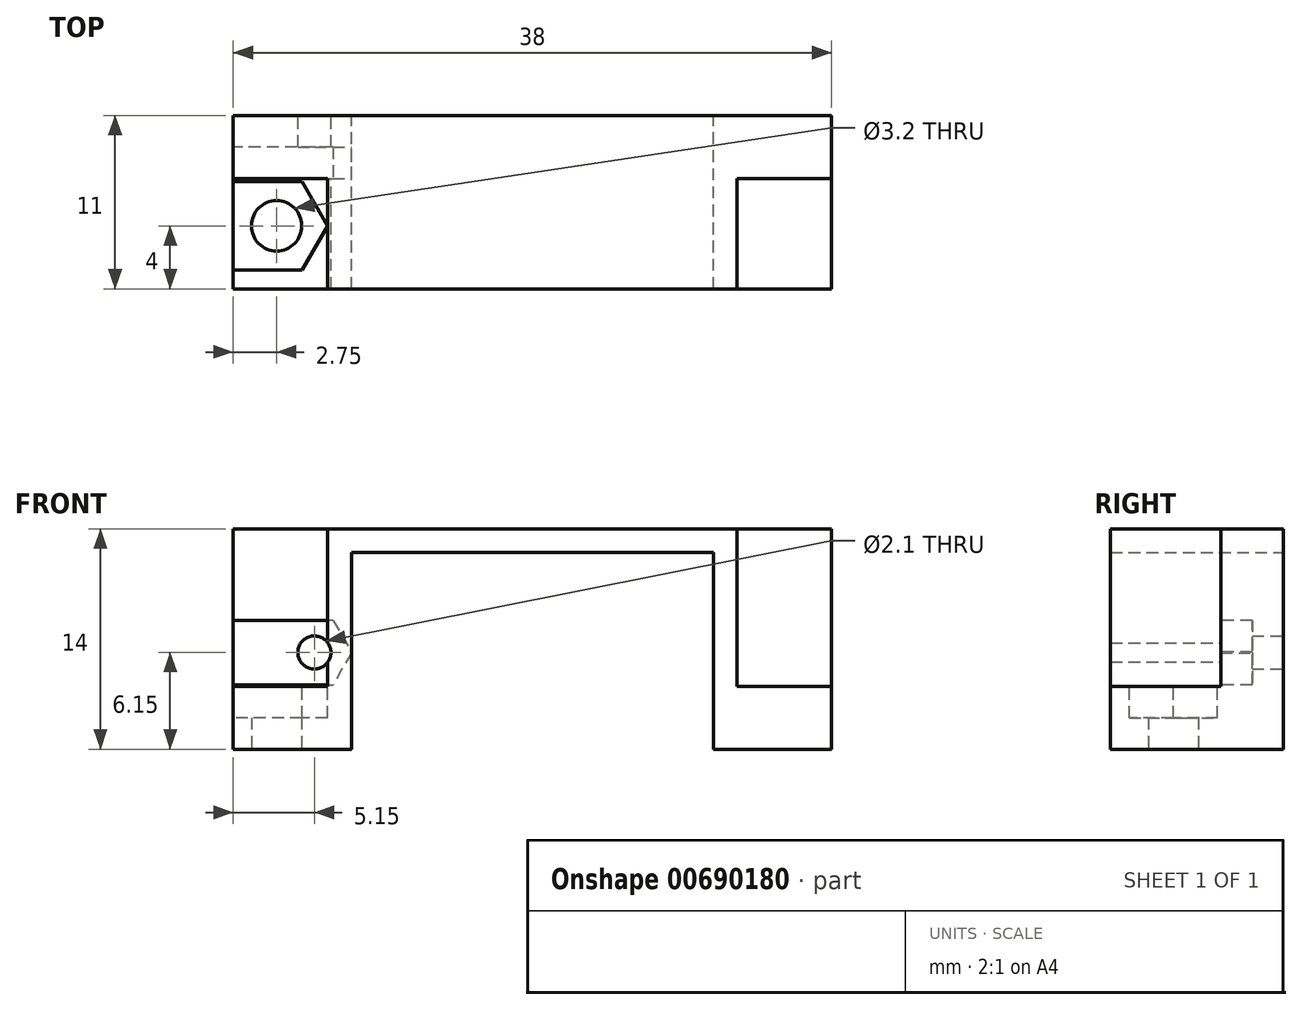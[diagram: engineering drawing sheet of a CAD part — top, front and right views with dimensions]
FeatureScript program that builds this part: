
annotation { "Feature Type Name" : "Feature", "Feature Type Description" : "" }
export const myFeature = defineFeature(function(context is Context, id is Id, definition is map)
    precondition{}
    {
        {
            var Q0;
            Q0=qCreatedBy(makeId("Front.planeOp"),FACE);
            var sketch = newSketch(context, id + "F0", { "sketchPlane" : qUnion([Q0])});
            skLineSegment(sketch, "E0", {"start": v(-19, 0) * mm, "end": v(-19, 4) * mm});
            skLineSegment(sketch, "E1", {"start": v(-19, 4) * mm, "end": v(-13, 4) * mm});
            skLineSegment(sketch, "E2", {"start": v(-13, 4) * mm, "end": v(-13, 14) * mm});
            skLineSegment(sketch, "E3", {"start": v(-13, 14) * mm, "end": v(13, 14) * mm});
            skLineSegment(sketch, "E4", {"start": v(13, 14) * mm, "end": v(13, 4) * mm});
            skLineSegment(sketch, "E5", {"start": v(13, 4) * mm, "end": v(19, 4) * mm});
            skLineSegment(sketch, "E6", {"start": v(19, 4) * mm, "end": v(19, 0) * mm});
            skLineSegment(sketch, "E7", {"start": v(19, 0) * mm, "end": v(11.5, 0) * mm});
            skLineSegment(sketch, "E8", {"start": v(-11.5, 0) * mm, "end": v(-11.5, 12.5) * mm});
            skLineSegment(sketch, "E9", {"start": v(-11.5, 12.5) * mm, "end": v(11.5, 12.5) * mm});
            skLineSegment(sketch, "E10", {"start": v(11.5, 12.5) * mm, "end": v(11.5, 0) * mm});
            skLineSegment(sketch, "E11.trimOffspring", {"start": v(-11.5, 0) * mm, "end": v(-19, 0) * mm});
            skSolve(sketch);
        }
        {
            var Q0;
            Q0=makeQuery(id+"F0.imprint","IMPRINT",FACE,{"disambiguationData":[TD([[makeQuery(id+"F0.imprint","IMPRINT",EDGE,{"derivedFrom":sQuery(id+"F0.wireOp",EDGE,"E0")}),-1.0]])]});
            extrude(context, id + "F1", {"entities" : qUnion([Q0]), "depth" : 11 * mm, "offsetDistance" : 25 * mm});
        }
        {
            var Q0;
            Q0=makeQuery(id+"F1.opExtrude","CAP_FACE",FACE,{"disambiguationData":[OSD([sQuery(id+"F0.wireOp",EDGE,"E0"),sQuery(id+"F0.wireOp",EDGE,"E1"),sQuery(id+"F0.wireOp",EDGE,"E2"),sQuery(id+"F0.wireOp",EDGE,"E3"),sQuery(id+"F0.wireOp",EDGE,"E4"),sQuery(id+"F0.wireOp",EDGE,"E5"),sQuery(id+"F0.wireOp",EDGE,"E6"),sQuery(id+"F0.wireOp",EDGE,"E7"),sQuery(id+"F0.wireOp",EDGE,"E8"),sQuery(id+"F0.wireOp",EDGE,"E9"),sQuery(id+"F0.wireOp",EDGE,"E10"),sQuery(id+"F0.wireOp",EDGE,"E11.trimOffspring")])],"isStart":true});
            var sketch = newSketch(context, id + "F2", { "sketchPlane" : qUnion([Q0])});
            skLineSegment(sketch, "E12.bottom", {"start": v(11.5, 0) * mm, "end": v(19, 0) * mm});
            skLineSegment(sketch, "E12.top", {"start": v(11.5, 14) * mm, "end": v(19, 14) * mm});
            skLineSegment(sketch, "E12.left", {"start": v(11.5, 0) * mm, "end": v(11.5, 14) * mm});
            skLineSegment(sketch, "E12.right", {"start": v(19, 0) * mm, "end": v(19, 14) * mm});
            skLineSegment(sketch, "E13.bottom", {"start": v(-11.5, 0) * mm, "end": v(-19, 0) * mm});
            skLineSegment(sketch, "E13.top", {"start": v(-11.5, 14) * mm, "end": v(-19, 14) * mm});
            skLineSegment(sketch, "E13.left", {"start": v(-11.5, 0) * mm, "end": v(-11.5, 14) * mm});
            skLineSegment(sketch, "E13.right", {"start": v(-19, 0) * mm, "end": v(-19, 14) * mm});
            skPoint(sketch, "E14", {"position": v(-13.85, 6.15) * mm});
            skPoint(sketch, "E15", {"position": v(13.85, 6.15) * mm});
            skSolve(sketch);
        }
        {
            var Q0;
            {var subQ1=makeQuery(id+"F1.opExtrude","CAP_EDGE",EDGE,{"disambiguationData":[OSD([sQuery(id+"F0.wireOp",EDGE,"E4")])],"isStart":true});Q0=makeQuery(id+"F2.imprint","IMPRINT",FACE,{"disambiguationData":[TD([[makeQuery(id+"F2.imprint","IMPRINT",EDGE,{"derivedFrom":subQ1}),-1.0]])]});}
            var Q1;
            {var subQ4=makeQuery(id+"F1.opExtrude","CAP_EDGE",EDGE,{"disambiguationData":[OSD([sQuery(id+"F0.wireOp",EDGE,"E1")])],"isStart":true});Q1=makeQuery(id+"F2.imprint","IMPRINT",FACE,{"disambiguationData":[TD([[makeQuery(id+"F2.imprint","IMPRINT",EDGE,{"derivedFrom":subQ4}),-1.0]])]});}
            extrude(context, id + "F3", {"entities" : qUnion([Q0, Q1]), "operationType" : NewBodyOperationType.ADD, "oppositeDirection" : true, "depth" : 4 * mm, "offsetDistance" : 25 * mm});
        }
        {
            var Q0;
            Q0=qCreatedBy(makeId("Front.planeOp"),FACE);
            var sketch = newSketch(context, id + "F4", { "sketchPlane" : qUnion([Q0])});
            skCircle(sketch, "E16", {"center": v(-13.85, 6.15) * mm, "radius": 1.05 * mm});
            skSolve(sketch);
        }
        {
            var Q0;
            Q0 = qSketchRegion(id + "F4", true);
            var Q1;
            Q1=makeQuery(id+"F1.opExtrude","CAP_FACE",FACE,{"disambiguationData":[OSD([sQuery(id+"F0.wireOp",EDGE,"E0"),sQuery(id+"F0.wireOp",EDGE,"E1"),sQuery(id+"F0.wireOp",EDGE,"E2"),sQuery(id+"F0.wireOp",EDGE,"E3"),sQuery(id+"F0.wireOp",EDGE,"E4"),sQuery(id+"F0.wireOp",EDGE,"E5"),sQuery(id+"F0.wireOp",EDGE,"E6"),sQuery(id+"F0.wireOp",EDGE,"E7"),sQuery(id+"F0.wireOp",EDGE,"E8"),sQuery(id+"F0.wireOp",EDGE,"E9"),sQuery(id+"F0.wireOp",EDGE,"E10"),sQuery(id+"F0.wireOp",EDGE,"E11.trimOffspring")])],"isStart":false});
            extrude(context, id + "F5", {"entities" : qUnion([Q0]), "operationType" : NewBodyOperationType.REMOVE, "endBound" : BoundingType.UP_TO_SURFACE, "depth" : 4 * mm, "endBoundEntityFace" : qUnion([Q1]), "offsetDistance" : 25 * mm});
        }
        {
            var Q0;
            Q0=makeQuery(id+"F3.opExtrude","CAP_FACE",FACE,{"disambiguationData":[OSD([sQuery(id+"F0.wireOp",EDGE,"E1"),sQuery(id+"F0.wireOp",EDGE,"E2"),sQuery(id+"F2.wireOp",EDGE,"E12.top"),sQuery(id+"F2.wireOp",EDGE,"E12.right")])],"isStart":false});
            var sketch = newSketch(context, id + "F6", { "sketchPlane" : qUnion([Q0])});
            skCircle(sketch, "E17.cCircle", {"center": v(-13.85, 6.15) * mm, "radius": 2.05 * mm, "construction": true});
            skLineSegment(sketch, "E17.0", {"start": v(-15.03, 8.2) * mm, "end": v(-12.67, 8.2) * mm});
            skLineSegment(sketch, "E17.1", {"start": v(-12.67, 8.2) * mm, "end": v(-11.48, 6.15) * mm});
            skLineSegment(sketch, "E17.2", {"start": v(-11.48, 6.15) * mm, "end": v(-12.67, 4.1) * mm});
            skLineSegment(sketch, "E17.3", {"start": v(-12.67, 4.1) * mm, "end": v(-15.03, 4.1) * mm});
            skLineSegment(sketch, "E17.4", {"start": v(-15.03, 4.1) * mm, "end": v(-16.22, 6.15) * mm});
            skLineSegment(sketch, "E17.5", {"start": v(-16.22, 6.15) * mm, "end": v(-15.03, 8.2) * mm});
            skPoint(sketch, "E17.0.midPoint", {"position": v(-13.85, 8.2) * mm});
            skLineSegment(sketch, "E18", {"start": v(-15.03, 8.2) * mm, "end": v(-19, 8.2) * mm});
            skLineSegment(sketch, "E19", {"start": v(-19, 8.2) * mm, "end": v(-19, 4.1) * mm});
            skLineSegment(sketch, "E20", {"start": v(-19, 4.1) * mm, "end": v(-15.03, 4.1) * mm});
            skSolve(sketch);
        }
        {
            var Q0;
            Q0 = qSketchRegion(id + "F6", true);
            extrude(context, id + "F7", {"entities" : qUnion([Q0]), "operationType" : NewBodyOperationType.REMOVE, "oppositeDirection" : true, "depth" : 2 * mm, "offsetDistance" : 25 * mm});
        }
        {
            var Q0;
            Q0=makeQuery(id+"F1.opExtrude","SWEPT_FACE",FACE,{"disambiguationData":[OSD([sQuery(id+"F0.wireOp",EDGE,"E11.trimOffspring")])]});
            var sketch = newSketch(context, id + "F8", { "sketchPlane" : qUnion([Q0])});
            skPoint(sketch, "E21", {"position": v(-16.25, 7) * mm});
            skCircle(sketch, "E22", {"center": v(-16.25, 7) * mm, "radius": 1.6 * mm});
            skLineSegment(sketch, "E23", {"start": v(-15.25, 11) * mm, "end": v(-15.25, 0) * mm, "construction": true});
            skSolve(sketch);
        }
        {
            var Q0;
            Q0=makeQuery(id+"F8.imprint","IMPRINT",FACE,{"disambiguationData":[TD([[makeQuery(id+"F8.imprint","IMPRINT",EDGE,{"derivedFrom":sQuery(id+"F8.wireOp",EDGE,"E22")}),1.0]])]});
            var Q1;
            Q1=makeQuery(id+"F1.opExtrude","SWEPT_FACE",FACE,{"disambiguationData":[OSD([sQuery(id+"F0.wireOp",EDGE,"E1")])]});
            extrude(context, id + "F9", {"entities" : qUnion([Q0]), "operationType" : NewBodyOperationType.REMOVE, "endBound" : BoundingType.UP_TO_SURFACE, "oppositeDirection" : true, "depth" : 25 * mm, "endBoundEntityFace" : qUnion([Q1]), "offsetDistance" : 25 * mm});
        }
        {
            var Q0;
            Q0=makeQuery(id+"F1.opExtrude","SWEPT_FACE",FACE,{"disambiguationData":[OSD([sQuery(id+"F0.wireOp",EDGE,"E1")])]});
            var sketch = newSketch(context, id + "F10", { "sketchPlane" : qUnion([Q0])});
            skCircle(sketch, "E24.cCircle", {"center": v(-16.25, -7) * mm, "radius": 2.8 * mm, "construction": true});
            skLineSegment(sketch, "E24.0", {"start": v(-17.87, -4.2) * mm, "end": v(-14.63, -4.2) * mm});
            skLineSegment(sketch, "E24.1", {"start": v(-14.63, -4.2) * mm, "end": v(-13.02, -7) * mm});
            skLineSegment(sketch, "E24.2", {"start": v(-13.02, -7) * mm, "end": v(-14.63, -9.8) * mm});
            skLineSegment(sketch, "E24.3", {"start": v(-14.63, -9.8) * mm, "end": v(-17.87, -9.8) * mm});
            skLineSegment(sketch, "E24.4", {"start": v(-17.87, -9.8) * mm, "end": v(-19.48, -7) * mm});
            skLineSegment(sketch, "E24.5", {"start": v(-19.48, -7) * mm, "end": v(-17.87, -4.2) * mm});
            skPoint(sketch, "E24.0.midPoint", {"position": v(-16.25, -4.2) * mm});
            skLineSegment(sketch, "E25", {"start": v(-17.87, -9.8) * mm, "end": v(-19, -9.8) * mm});
            skLineSegment(sketch, "E26", {"start": v(-19, -9.8) * mm, "end": v(-19, -4.2) * mm});
            skLineSegment(sketch, "E27", {"start": v(-19, -4.2) * mm, "end": v(-17.87, -4.2) * mm});
            skSolve(sketch);
        }
        {
            var Q0;
            Q0 = qSketchRegion(id + "F10", true);
            extrude(context, id + "F11", {"entities" : qUnion([Q0]), "operationType" : NewBodyOperationType.REMOVE, "oppositeDirection" : true, "depth" : 2 * mm, "offsetDistance" : 25 * mm});
        }
    });
